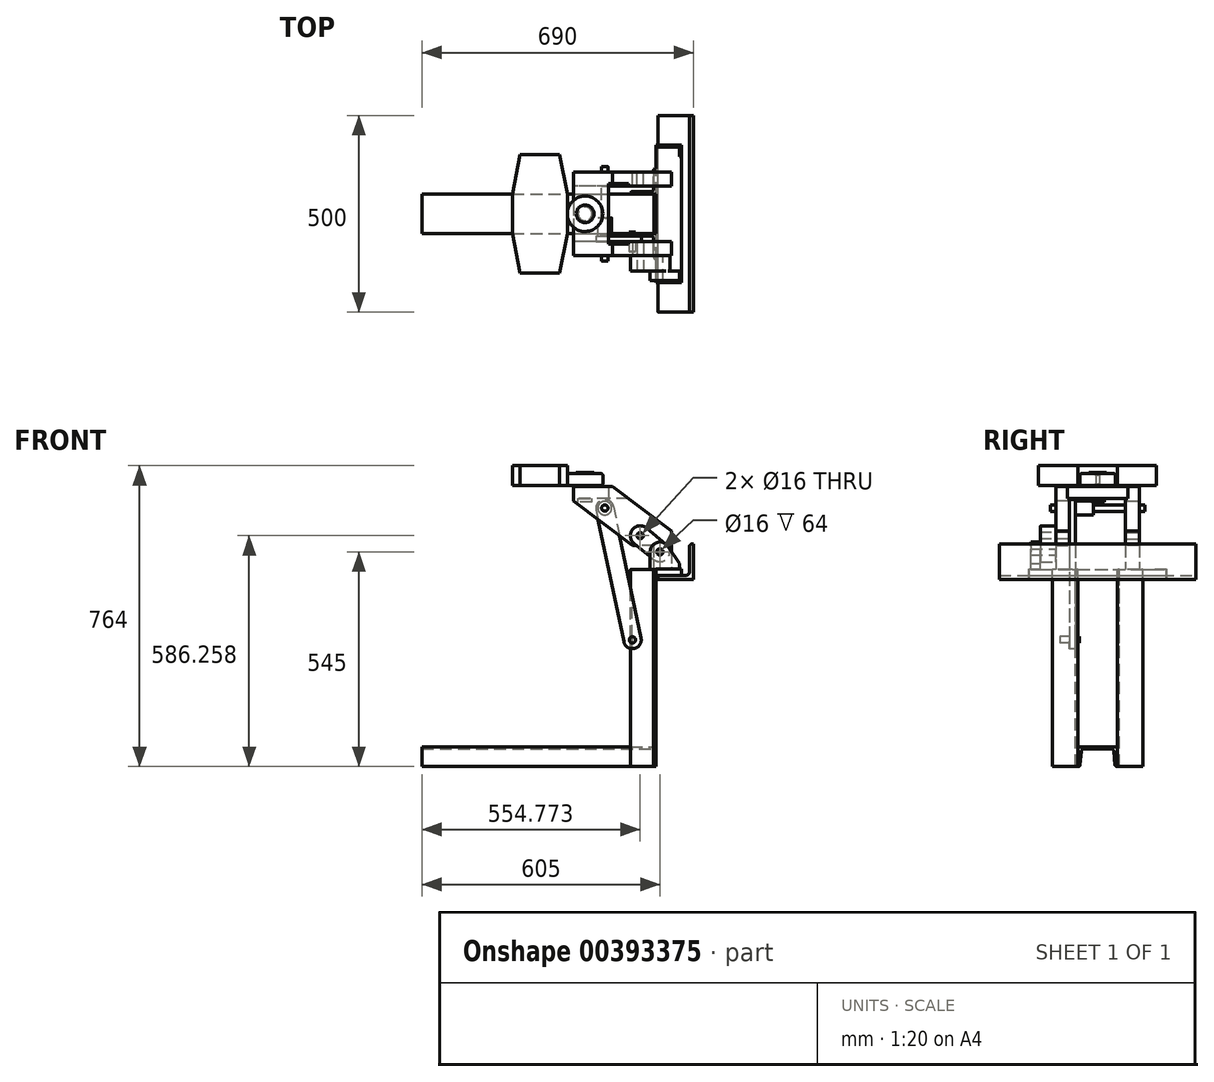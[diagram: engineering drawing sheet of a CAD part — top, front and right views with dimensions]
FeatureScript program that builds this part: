
annotation { "Feature Type Name" : "Feature", "Feature Type Description" : "" }
export const myFeature = defineFeature(function(context is Context, id is Id, definition is map)
    precondition{}
    {
        {
            var Q0;
            Q0=qCreatedBy(makeId("Front.planeOp"),FACE);
            var sketch = newSketch(context, id + "F0", { "sketchPlane" : qUnion([Q0])});
            skLineSegment(sketch, "E0", {"start": v(0, 0) * mm, "end": v(0, 90) * mm});
            skLineSegment(sketch, "E1", {"start": v(0, 90) * mm, "end": v(-3, 90) * mm});
            skLineSegment(sketch, "E2", {"start": v(-10, 83) * mm, "end": v(-10, 20) * mm});
            skLineSegment(sketch, "E3", {"start": v(-20, 10) * mm, "end": v(-83, 10) * mm});
            skLineSegment(sketch, "E4", {"start": v(-90, 3) * mm, "end": v(-90, 0) * mm});
            skLineSegment(sketch, "E5", {"start": v(-90, 0) * mm, "end": v(0, 0) * mm});
            skPoint(sketch, "E6.visualSharp", {"position": v(-10, 90) * mm});
            skArc(sketch, "E6.filletArc", {"start": v(-3, 90) * mm, "mid": v(-7.95, 87.95) * mm, "end": v(-10, 83) * mm});
            skPoint(sketch, "E7.visualSharp", {"position": v(-90, 10) * mm});
            skArc(sketch, "E7.filletArc", {"start": v(-83, 10) * mm, "mid": v(-87.95, 7.95) * mm, "end": v(-90, 3) * mm});
            skPoint(sketch, "E8.visualSharp", {"position": v(-10, 10) * mm});
            skArc(sketch, "E8.filletArc", {"start": v(-20, 10) * mm, "mid": v(-12.93, 12.93) * mm, "end": v(-10, 20) * mm});
            skLineSegment(sketch, "E9", {"start": v(-90, 0) * mm, "end": v(-95, 0) * mm});
            skLineSegment(sketch, "E10", {"start": v(-95, 0) * mm, "end": v(-95, 25) * mm});
            skLineSegment(sketch, "E11", {"start": v(-95, 25) * mm, "end": v(-30, 25) * mm});
            skLineSegment(sketch, "E12", {"start": v(-30, 25) * mm, "end": v(-30, 10) * mm});
            skLineSegment(sketch, "E13", {"start": v(-30, 10) * mm, "end": v(-90, 10) * mm});
            skLineSegment(sketch, "E14", {"start": v(-90, 0) * mm, "end": v(-90, 10) * mm});
            skLineSegment(sketch, "E15", {"start": v(-35, 25) * mm, "end": v(-35, 40) * mm});
            skLineSegment(sketch, "E16", {"start": v(-95, 25) * mm, "end": v(-110, 25) * mm});
            skLineSegment(sketch, "E17", {"start": v(-110, 25) * mm, "end": v(-110, 70) * mm});
            skCircle(sketch, "E18", {"center": v(-85, 70) * mm, "radius": 25 * mm});
            skLineSegment(sketch, "E19", {"start": v(-35, 40) * mm, "end": v(-64.19, 83.85) * mm});
            skCircle(sketch, "E20", {"center": v(-85, 70) * mm, "radius": 8 * mm});
            skSolve(sketch);
        }
        {
            var Q0;
            Q0=makeQuery(id+"F0.imprint","IMPRINT",FACE,{"disambiguationData":[TD([[makeQuery(id+"F0.imprint","IMPRINT",EDGE,{"derivedFrom":sQuery(id+"F0.wireOp",EDGE,"E0")}),1.0]])]});
            extrude(context, id + "F1", {"entities" : qUnion([Q0]), "endBound" : BoundingType.SYMMETRIC, "depth" : 500 * mm});
        }
        {
            var Q0;
            {var subQ4=sQuery(id+"F0.wireOp",EDGE,"E9");Q0=makeQuery(id+"F0.imprint","IMPRINT",FACE,{"disambiguationData":[TD([[makeQuery(id+"F0.imprint","IMPRINT",EDGE,{"derivedFrom":subQ4}),-1.0]])]});}
            extrude(context, id + "F2", {"entities" : qUnion([Q0]), "endBound" : BoundingType.SYMMETRIC, "depth" : 350 * mm});
        }
        {
            var Q0;
            {var subQ2=sQuery(id+"F0.wireOp",EDGE,"E15");Q0=makeQuery(id+"F0.imprint","IMPRINT",FACE,{"disambiguationData":[TD([[makeQuery(id+"F0.imprint","IMPRINT",EDGE,{"derivedFrom":subQ2}),1.0]])]});}
            var Q1;
            Q1=makeQuery(id+"F0.imprint","IMPRINT",FACE,{"disambiguationData":[TD([[makeQuery(id+"F0.imprint","IMPRINT",EDGE,{"derivedFrom":sQuery(id+"F0.wireOp",EDGE,"E20")}),-1.0]])]});
            extrude(context, id + "F3", {"entities" : qUnion([Q0, Q1]), "depth" : 170 * mm, "hasSecondDirection" : true, "secondDirectionOppositeDirection" : false, "secondDirectionDepth" : 145 * mm});
        }
        {
            var Q0;
            Q0=makeQuery(id+"F3.opExtrude","CAP_FACE",FACE,{"disambiguationData":[OSD([sQuery(id+"F0.wireOp",EDGE,"E11"),sQuery(id+"F0.wireOp",EDGE,"E15"),sQuery(id+"F0.wireOp",EDGE,"E16"),sQuery(id+"F0.wireOp",EDGE,"E17"),sQuery(id+"F0.wireOp",EDGE,"E18"),sQuery(id+"F0.wireOp",EDGE,"E19"),sQuery(id+"F0.wireOp",EDGE,"E20")])],"isStart":true});
            var sketch = newSketch(context, id + "F4", { "sketchPlane" : qUnion([Q0])});
            skCircle(sketch, "E21.0", {"center": v(85, 70) * mm, "radius": 8 * mm});
            skLineSegment(sketch, "E22", {"start": v(85, 70) * mm, "end": v(135.23, 111.26) * mm, "construction": true});
            skCircle(sketch, "E23", {"center": v(135.23, 111.26) * mm, "radius": 8 * mm});
            skArc(sketch, "E24", {"start": v(151.1, 91.94) * mm, "mid": v(154.55, 127.13) * mm, "end": v(119.36, 130.58) * mm});
            skArc(sketch, "E25", {"start": v(110, 70) * mm, "mid": v(62.4, 80.68) * mm, "end": v(100.87, 50.68) * mm});
            skArc(sketch, "E26.0", {"start": v(64.19, 83.85) * mm, "mid": v(92.24, 93.93) * mm, "end": v(110, 70) * mm});
            skLineSegment(sketch, "E27", {"start": v(119.36, 130.58) * mm, "end": v(69.13, 89.32) * mm});
            skLineSegment(sketch, "E28", {"start": v(151.1, 91.94) * mm, "end": v(100.87, 50.68) * mm});
            skSolve(sketch);
        }
        {
            var Q0;
            Q0=makeQuery(id+"F4.imprint","IMPRINT",FACE,{"disambiguationData":[TD([[makeQuery(id+"F4.imprint","IMPRINT",EDGE,{"derivedFrom":sQuery(id+"F4.wireOp",EDGE,"E21.0")}),1.0]])]});
            var Q1;
            Q1=makeQuery(id+"F4.imprint","IMPRINT",FACE,{"disambiguationData":[TD([[makeQuery(id+"F4.imprint","IMPRINT",EDGE,{"derivedFrom":sQuery(id+"F4.wireOp",EDGE,"E23")}),-1.0]])]});
            extrude(context, id + "F5", {"entities" : qUnion([Q0, Q1]), "depth" : 39 * mm});
        }
        {
            var Q0;
            Q0=makeQuery(id+"F5.opExtrude","CAP_FACE",FACE,{"disambiguationData":[OSD([sQuery(id+"F4.wireOp",EDGE,"E21.0"),sQuery(id+"F4.wireOp",EDGE,"E23"),sQuery(id+"F4.wireOp",EDGE,"E24"),sQuery(id+"F4.wireOp",EDGE,"E25"),sQuery(id+"F4.wireOp",EDGE,"E26.0"),sQuery(id+"F4.wireOp",EDGE,"E27"),sQuery(id+"F4.wireOp",EDGE,"E28")])],"isStart":false});
            var sketch = newSketch(context, id + "F6", { "sketchPlane" : qUnion([Q0])});
            skCircle(sketch, "E29.0", {"center": v(135.23, 111.26) * mm, "radius": 8 * mm});
            skLineSegment(sketch, "E30", {"start": v(135.23, 111.26) * mm, "end": v(225.23, 181.26) * mm, "construction": true});
            skCircle(sketch, "E31", {"center": v(225.23, 181.26) * mm, "radius": 8 * mm});
            skLineSegment(sketch, "E32", {"start": v(55.23, 86.26) * mm, "end": v(155.23, 86.26) * mm});
            skLineSegment(sketch, "E33", {"start": v(155.23, 86.26) * mm, "end": v(305.23, 198.76) * mm});
            skLineSegment(sketch, "E34", {"start": v(305.23, 198.76) * mm, "end": v(305.23, 236.26) * mm});
            skLineSegment(sketch, "E35", {"start": v(305.23, 236.26) * mm, "end": v(205.23, 236.26) * mm});
            skLineSegment(sketch, "E36", {"start": v(205.23, 236.26) * mm, "end": v(55.23, 123.76) * mm});
            skLineSegment(sketch, "E37", {"start": v(55.23, 123.76) * mm, "end": v(55.23, 86.26) * mm});
            skSolve(sketch);
        }
        {
            var Q0;
            Q0=makeQuery(id+"F6.imprint","IMPRINT",FACE,{"disambiguationData":[TD([[makeQuery(id+"F6.imprint","IMPRINT",EDGE,{"derivedFrom":sQuery(id+"F6.wireOp",EDGE,"E31")}),-1.0]])]});
            var Q1;
            Q1=makeQuery(id+"F6.imprint","IMPRINT",FACE,{"disambiguationData":[TD([[makeQuery(id+"F6.imprint","IMPRINT",EDGE,{"derivedFrom":sQuery(id+"F6.wireOp",EDGE,"E29.0")}),-1.0]])]});
            extrude(context, id + "F7", {"entities" : qUnion([Q0, Q1]), "depth" : 35 * mm});
        }
        {
            var Q0;
            Q0=makeQuery(id+"F7.opExtrude","SWEPT_FACE",FACE,{"disambiguationData":[OSD([sQuery(id+"F6.wireOp",EDGE,"E34")])]});
            var sketch = newSketch(context, id + "F8", { "sketchPlane" : qUnion([Q0])});
            skLineSegment(sketch, "E38.0", {"start": v(71, 236.26) * mm, "end": v(106, 236.26) * mm});
            skLineSegment(sketch, "E39.0", {"start": v(71, 198.76) * mm, "end": v(71, 236.26) * mm});
            skLineSegment(sketch, "E40", {"start": v(76.5, 236.26) * mm, "end": v(76.5, 206.26) * mm});
            skLineSegment(sketch, "E41", {"start": v(76.5, 206.26) * mm, "end": v(71, 206.26) * mm});
            skSolve(sketch);
        }
        {
            var Q0;
            {var subQ3=sQuery(id+"F8.wireOp",EDGE,"E40");Q0=makeQuery(id+"F8.imprint","IMPRINT",FACE,{"disambiguationData":[TD([[makeQuery(id+"F8.imprint","IMPRINT",EDGE,{"derivedFrom":subQ3}),-1.0]])]});}
            extrude(context, id + "F9", {"entities" : qUnion([Q0]), "operationType" : NewBodyOperationType.REMOVE, "endBound" : BoundingType.THROUGH_ALL, "oppositeDirection" : true, "depth" : 25 * mm});
        }
        {
            var Q0;
            Q0=makeQuery(id+"F7.opExtrude","SWEPT_FACE",FACE,{"disambiguationData":[OSD([sQuery(id+"F6.wireOp",EDGE,"E34")])]});
            var sketch = newSketch(context, id + "F10", { "sketchPlane" : qUnion([Q0])});
            skLineSegment(sketch, "E42.0", {"start": v(76.5, 236.26) * mm, "end": v(76.5, 206.26) * mm});
            skLineSegment(sketch, "E43.0", {"start": v(76.5, 206.26) * mm, "end": v(71, 206.26) * mm});
            skLineSegment(sketch, "E44", {"start": v(76.5, 236.26) * mm, "end": v(-76.5, 236.26) * mm});
            skLineSegment(sketch, "E45", {"start": v(-76.5, 236.26) * mm, "end": v(-76.5, 206.26) * mm});
            skLineSegment(sketch, "E46", {"start": v(-76.5, 206.26) * mm, "end": v(71, 206.26) * mm});
            skPoint(sketch, "E47", {"position": v(0, 236.26) * mm});
            skSolve(sketch);
        }
        {
            var Q0;
            Q0=makeQuery(id+"F10.imprint","IMPRINT",FACE,{"disambiguationData":[TD([[makeQuery(id+"F10.imprint","IMPRINT",EDGE,{"derivedFrom":sQuery(id+"F10.wireOp",EDGE,"E42.0")}),-1.0]])]});
            extrude(context, id + "F11", {"entities" : qUnion([Q0]), "oppositeDirection" : true, "depth" : 90 * mm});
        }
        {
            var Q0;
            Q0=makeQuery(id+"F11.opExtrude","SWEPT_FACE",FACE,{"disambiguationData":[OSD([sQuery(id+"F10.wireOp",EDGE,"E44")])]});
            var sketch = newSketch(context, id + "F12", { "sketchPlane" : qUnion([Q0])});
            skCircle(sketch, "E48", {"center": v(-275.23, 0) * mm, "radius": 17.5 * mm});
            skSolve(sketch);
        }
        {
            var Q0;
            Q0=makeQuery(id+"F12.imprint","IMPRINT",FACE,{"disambiguationData":[TD([[makeQuery(id+"F12.imprint","IMPRINT",EDGE,{"derivedFrom":sQuery(id+"F12.wireOp",EDGE,"E48")}),1.0]])]});
            extrude(context, id + "F13", {"entities" : qUnion([Q0]), "operationType" : NewBodyOperationType.REMOVE, "endBound" : BoundingType.THROUGH_ALL, "oppositeDirection" : true, "depth" : 25 * mm});
        }
        {
            var Q0;
            Q0=makeQuery(id+"F11.opExtrude","SWEPT_FACE",FACE,{"disambiguationData":[OSD([sQuery(id+"F10.wireOp",EDGE,"E44")])]});
            var sketch = newSketch(context, id + "F14", { "sketchPlane" : qUnion([Q0])});
            skCircle(sketch, "E49.0", {"center": v(-275.23, 0) * mm, "radius": 17.5 * mm});
            skCircle(sketch, "E50", {"center": v(-275.23, 0) * mm, "radius": 22.5 * mm});
            skCircle(sketch, "E51", {"center": v(-275.23, 0) * mm, "radius": 45 * mm});
            skSolve(sketch);
        }
        {
            var Q0;
            Q0=makeQuery(id+"F14.imprint","IMPRINT",FACE,{"disambiguationData":[TD([[makeQuery(id+"F14.imprint","IMPRINT",EDGE,{"derivedFrom":sQuery(id+"F14.wireOp",EDGE,"E49.0")}),1.0]])]});
            extrude(context, id + "F15", {"entities" : qUnion([Q0]), "oppositeDirection" : true, "depth" : 40 * mm});
        }
        {
            var Q0;
            Q0=makeQuery(id+"F14.imprint","IMPRINT",FACE,{"disambiguationData":[TD([[makeQuery(id+"F14.imprint","IMPRINT",EDGE,{"derivedFrom":sQuery(id+"F14.wireOp",EDGE,"E49.0")}),1.0]])]});
            var Q1;
            Q1=makeQuery(id+"F14.imprint","IMPRINT",FACE,{"disambiguationData":[TD([[makeQuery(id+"F14.imprint","IMPRINT",EDGE,{"derivedFrom":sQuery(id+"F14.wireOp",EDGE,"E49.0")}),-1.0]])]});
            extrude(context, id + "F16", {"entities" : qUnion([Q0, Q1]), "operationType" : NewBodyOperationType.ADD, "depth" : 35 * mm});
        }
        {
            var Q0;
            Q0=makeQuery(id+"F14.imprint","IMPRINT",FACE,{"disambiguationData":[TD([[makeQuery(id+"F14.imprint","IMPRINT",EDGE,{"derivedFrom":sQuery(id+"F14.wireOp",EDGE,"E50")}),-1.0]])]});
            var Q1;
            {var subQ0=sQuery(id+"F14.wireOp",EDGE,"E51");var subQ1=makeQuery(id+"F11.opExtrude","CAP_EDGE",EDGE,{"disambiguationData":[OSD([sQuery(id+"F10.wireOp",EDGE,"E44")])],"isStart":true});var subQ2=makeQuery(id+"F14.imprint","INTERSECT",VERTEX,{"disambiguationData":[OD(0.0)],"derivedFrom":[subQ1,subQ0]});Q1=makeQuery(id+"F14.imprint","IMPRINT",FACE,{"disambiguationData":[TD([[makeQuery(id+"F14.imprint","IMPRINT",EDGE,{"disambiguationData":[TD([[subQ2,1.0]])],"derivedFrom":subQ0}),1.0]])]});}
            var Q2;
            Q2=makeQuery(id+"F14.imprint","IMPRINT",FACE,{"disambiguationData":[TD([[makeQuery(id+"F14.imprint","IMPRINT",EDGE,{"derivedFrom":sQuery(id+"F14.wireOp",EDGE,"E49.0")}),-1.0]])]});
            var Q3;
            Q3=makeQuery(id+"F14.imprint","IMPRINT",FACE,{"disambiguationData":[TD([[makeQuery(id+"F14.imprint","IMPRINT",EDGE,{"derivedFrom":sQuery(id+"F14.wireOp",EDGE,"E49.0")}),1.0]])]});
            extrude(context, id + "F17", {"entities" : qUnion([Q0, Q1, Q2, Q3]), "operationType" : NewBodyOperationType.ADD, "depth" : 33 * mm, "hasSecondDirection" : true, "secondDirectionOppositeDirection" : false, "secondDirectionDepth" : 2 * mm});
        }
        {
            var Q0;
            Q0=makeQuery(id+"F17.opExtrude","CAP_EDGE",EDGE,{"disambiguationData":[OSD([sQuery(id+"F14.wireOp",EDGE,"E51")])],"isStart":false});
            var Q1;
            Q1=makeQuery(id+"F17.opExtrude","CAP_EDGE",EDGE,{"disambiguationData":[OSD([sQuery(id+"F14.wireOp",EDGE,"E51")])],"isStart":true});
            fillet(context, id + "F18", {"entities" : qUnion([Q0, Q1]), "radius" : 5 * mm, "tangentPropagation" : true, "allowEdgeOverflow" : false});
        }
        {
            var Q0;
            Q0=makeQuery(id+"F7.opExtrude","CAP_FACE",FACE,{"disambiguationData":[OSD([sQuery(id+"F6.wireOp",EDGE,"E29.0"),sQuery(id+"F6.wireOp",EDGE,"E31"),sQuery(id+"F6.wireOp",EDGE,"E32"),sQuery(id+"F6.wireOp",EDGE,"E33"),sQuery(id+"F6.wireOp",EDGE,"E34"),sQuery(id+"F6.wireOp",EDGE,"E35"),sQuery(id+"F6.wireOp",EDGE,"E36"),sQuery(id+"F6.wireOp",EDGE,"E37")])],"isStart":false});
            var sketch = newSketch(context, id + "F19", { "sketchPlane" : qUnion([Q0])});
            skLineSegment(sketch, "E52", {"start": v(225.23, 181.26) * mm, "end": v(155, -153.45) * mm, "construction": true});
            skCircle(sketch, "E53.0", {"center": v(85, 70) * mm, "radius": 8 * mm});
            skCircle(sketch, "E54", {"center": v(225.23, 181.26) * mm, "radius": 8 * mm});
            skArc(sketch, "E55", {"start": v(247.25, 176.64) * mm, "mid": v(229.85, 203.28) * mm, "end": v(203.2, 185.88) * mm});
            skCircle(sketch, "E56", {"center": v(155, -153.45) * mm, "radius": 8 * mm});
            skArc(sketch, "E57", {"start": v(132.98, -148.83) * mm, "mid": v(150.38, -175.47) * mm, "end": v(177.02, -158.07) * mm});
            skLineSegment(sketch, "E58", {"start": v(203.2, 185.88) * mm, "end": v(132.98, -148.83) * mm});
            skLineSegment(sketch, "E59", {"start": v(247.25, 176.64) * mm, "end": v(177.02, -158.07) * mm});
            skSolve(sketch);
        }
        {
            var Q0;
            Q0=makeQuery(id+"F19.imprint","IMPRINT",FACE,{"disambiguationData":[TD([[makeQuery(id+"F19.imprint","IMPRINT",EDGE,{"derivedFrom":sQuery(id+"F19.wireOp",EDGE,"E56")}),-1.0]])]});
            var Q1;
            Q1=makeQuery(id+"F19.imprint","IMPRINT",FACE,{"disambiguationData":[TD([[makeQuery(id+"F19.imprint","IMPRINT",EDGE,{"derivedFrom":sQuery(id+"F19.wireOp",EDGE,"E54")}),-1.0]])]});
            extrude(context, id + "F20", {"entities" : qUnion([Q0, Q1]), "depth" : 15 * mm});
        }
        {
            var Q0;
            Q0=qCreatedBy(makeId("Front.planeOp"),FACE);
            var sketch = newSketch(context, id + "F21", { "sketchPlane" : qUnion([Q0])});
            skCircle(sketch, "E60.0", {"center": v(-225.23, 181.26) * mm, "radius": 8 * mm});
            skCircle(sketch, "E61", {"center": v(-225.23, 181.26) * mm, "radius": 17.5 * mm});
            skSolve(sketch);
        }
        {
            var Q0;
            Q0=makeQuery(id+"F21.imprint","IMPRINT",FACE,{"disambiguationData":[TD([[makeQuery(id+"F21.imprint","IMPRINT",EDGE,{"derivedFrom":sQuery(id+"F21.wireOp",EDGE,"E60.0")}),1.0]])]});
            extrude(context, id + "F22", {"entities" : qUnion([Q0]), "endBound" : BoundingType.SYMMETRIC, "depth" : 240 * mm});
        }
        {
            var Q0;
            Q0=makeQuery(id+"F21.imprint","IMPRINT",FACE,{"disambiguationData":[TD([[makeQuery(id+"F21.imprint","IMPRINT",EDGE,{"derivedFrom":sQuery(id+"F21.wireOp",EDGE,"E60.0")}),-1.0]])]});
            var Q1;
            Q1=makeQuery(id+"F7.opExtrude","CAP_FACE",FACE,{"disambiguationData":[OSD([sQuery(id+"F6.wireOp",EDGE,"E29.0"),sQuery(id+"F6.wireOp",EDGE,"E31"),sQuery(id+"F6.wireOp",EDGE,"E32"),sQuery(id+"F6.wireOp",EDGE,"E33"),sQuery(id+"F6.wireOp",EDGE,"E34"),sQuery(id+"F6.wireOp",EDGE,"E35"),sQuery(id+"F6.wireOp",EDGE,"E36"),sQuery(id+"F6.wireOp",EDGE,"E37")])],"isStart":false});
            extrude(context, id + "F23", {"entities" : qUnion([Q0]), "endBound" : BoundingType.UP_TO_SURFACE, "endBoundEntityFace" : qUnion([Q1]), "depth" : 25 * mm, "hasSecondDirection" : true, "secondDirectionOppositeDirection" : false, "secondDirectionDepth" : 10.5 * mm});
        }
        {
            var Q0;
            Q0=makeQuery(id+"F11.opExtrude","SWEPT_FACE",FACE,{"disambiguationData":[OSD([sQuery(id+"F10.wireOp",EDGE,"E45")])]});
            var sketch = newSketch(context, id + "F24", { "sketchPlane" : qUnion([Q0])});
            skLineSegment(sketch, "E62.0", {"start": v(205.23, 236.26) * mm, "end": v(305.23, 236.26) * mm});
            skLineSegment(sketch, "E63.0", {"start": v(165.23, 206.26) * mm, "end": v(305.23, 206.26) * mm});
            skLineSegment(sketch, "E64.0", {"start": v(205.23, 236.26) * mm, "end": v(165.23, 206.26) * mm});
            skLineSegment(sketch, "E65.0", {"start": v(305.23, 236.26) * mm, "end": v(305.23, 206.26) * mm});
            skLineSegment(sketch, "E66.0", {"start": v(305.23, 198.76) * mm, "end": v(305.23, 206.26) * mm});
            skLineSegment(sketch, "E67.0", {"start": v(155.23, 86.26) * mm, "end": v(305.23, 198.76) * mm});
            skLineSegment(sketch, "E68.0", {"start": v(205.23, 236.26) * mm, "end": v(55.23, 123.76) * mm});
            skLineSegment(sketch, "E69.0", {"start": v(55.23, 123.76) * mm, "end": v(55.23, 86.26) * mm});
            skLineSegment(sketch, "E70.0", {"start": v(55.23, 86.26) * mm, "end": v(155.23, 86.26) * mm});
            skCircle(sketch, "E71.0", {"center": v(225.23, 181.26) * mm, "radius": 8 * mm});
            skCircle(sketch, "E72.0", {"center": v(135.23, 111.26) * mm, "radius": 8 * mm});
            skSolve(sketch);
        }
        {
            var Q0;
            {var subQ0=sQuery(id+"F24.wireOp",EDGE,"E66.0");Q0=makeQuery(id+"F24.imprint","IMPRINT",FACE,{"disambiguationData":[TD([[makeQuery(id+"F24.imprint","IMPRINT",EDGE,{"derivedFrom":subQ0}),1.0]])]});}
            extrude(context, id + "F25", {"entities" : qUnion([Q0]), "oppositeDirection" : true, "depth" : 5.5 * mm});
        }
        {
            var Q0;
            {var subQ0=sQuery(id+"F24.wireOp",EDGE,"E66.0");Q0=makeQuery(id+"F24.imprint","IMPRINT",FACE,{"disambiguationData":[TD([[makeQuery(id+"F24.imprint","IMPRINT",EDGE,{"derivedFrom":subQ0}),1.0]])]});}
            var Q1;
            {var subQ1=makeQuery(id+"F11.opExtrude","CAP_EDGE",EDGE,{"disambiguationData":[OSD([sQuery(id+"F10.wireOp",EDGE,"E45")])],"isStart":false});Q1=makeQuery(id+"F24.imprint","IMPRINT",FACE,{"disambiguationData":[TD([[makeQuery(id+"F24.imprint","IMPRINT",EDGE,{"derivedFrom":subQ1}),-1.0]])]});}
            var Q2;
            {var subQ0=sQuery(id+"F24.wireOp",EDGE,"E65.0");Q2=makeQuery(id+"F24.imprint","IMPRINT",FACE,{"disambiguationData":[TD([[makeQuery(id+"F24.imprint","IMPRINT",EDGE,{"derivedFrom":subQ0}),-1.0]])]});}
            extrude(context, id + "F26", {"entities" : qUnion([Q0, Q1, Q2]), "operationType" : NewBodyOperationType.ADD, "depth" : 29.5 * mm});
        }
        {
            var Q0;
            Q0=makeQuery(id+"F2.opExtrude","SWEPT_FACE",FACE,{"disambiguationData":[OSD([sQuery(id+"F0.wireOp",EDGE,"E11")])]});
            var sketch = newSketch(context, id + "F27", { "sketchPlane" : qUnion([Q0])});
            skLineSegment(sketch, "E73.0", {"start": v(-35, -170) * mm, "end": v(-110, -170) * mm});
            skLineSegment(sketch, "E74.0", {"start": v(-35, -170) * mm, "end": v(-35, -145) * mm});
            skLineSegment(sketch, "E75.0", {"start": v(-30, -175) * mm, "end": v(-30, 175) * mm});
            skLineSegment(sketch, "E76.0", {"start": v(-95, -175) * mm, "end": v(-30, -175) * mm});
            skLineSegment(sketch, "E77.0", {"start": v(-95, -175) * mm, "end": v(-95, 175) * mm});
            skLineSegment(sketch, "E78.0", {"start": v(-95, 175) * mm, "end": v(-30, 175) * mm});
            skLineSegment(sketch, "E79", {"start": v(-35, 145) * mm, "end": v(-35, 170) * mm});
            skLineSegment(sketch, "E80", {"start": v(-35, 170) * mm, "end": v(-110, 170) * mm});
            skLineSegment(sketch, "E81", {"start": v(-35, -145) * mm, "end": v(-30, -145) * mm});
            skLineSegment(sketch, "E82", {"start": v(-35, 145) * mm, "end": v(-30, 145) * mm});
            skSolve(sketch);
        }
        {
            var Q0;
            {var subQ3=sQuery(id+"F27.wireOp",EDGE,"E74.0");Q0=makeQuery(id+"F27.imprint","IMPRINT",FACE,{"disambiguationData":[TD([[makeQuery(id+"F27.imprint","IMPRINT",EDGE,{"derivedFrom":subQ3}),-1.0]])]});}
            var Q1;
            {var subQ1=sQuery(id+"F27.wireOp",EDGE,"E78.0");Q1=makeQuery(id+"F27.imprint","IMPRINT",FACE,{"disambiguationData":[TD([[makeQuery(id+"F27.imprint","IMPRINT",EDGE,{"derivedFrom":subQ1}),-1.0]])]});}
            extrude(context, id + "F28", {"entities" : qUnion([Q0, Q1]), "operationType" : NewBodyOperationType.ADD, "depth" : 1 * mm});
        }
        {
            var Q0;
            Q0=makeQuery(id+"F2.opExtrude","SWEPT_FACE",FACE,{"disambiguationData":[OSD([sQuery(id+"F0.wireOp",EDGE,"E11")])]});
            var sketch = newSketch(context, id + "F29", { "sketchPlane" : qUnion([Q0])});
            skLineSegment(sketch, "E83.0", {"start": v(-95, -50) * mm, "end": v(-95, 115) * mm});
            skLineSegment(sketch, "E84", {"start": v(-95, 50) * mm, "end": v(-95, -50) * mm, "construction": true});
            skPoint(sketch, "E85", {"position": v(-95, 0) * mm});
            skLineSegment(sketch, "E86", {"start": v(-95, 50) * mm, "end": v(-160, 50) * mm});
            skLineSegment(sketch, "E87", {"start": v(-160, 50) * mm, "end": v(-160, 52) * mm});
            skLineSegment(sketch, "E88", {"start": v(-156, 56) * mm, "end": v(-109, 56) * mm});
            skLineSegment(sketch, "E89", {"start": v(-101, 64) * mm, "end": v(-101, 111) * mm});
            skLineSegment(sketch, "E90", {"start": v(-97, 115) * mm, "end": v(-95, 115) * mm});
            skPoint(sketch, "E91.orphan", {"position": v(-95, 170) * mm});
            skPoint(sketch, "E92.orphan", {"position": v(-95, -170) * mm});
            skPoint(sketch, "E93.visualSharp", {"position": v(-101, 56) * mm});
            skArc(sketch, "E93.filletArc", {"start": v(-109, 56) * mm, "mid": v(-103.34, 58.34) * mm, "end": v(-101, 64) * mm});
            skPoint(sketch, "E94.visualSharp", {"position": v(-101, 115) * mm});
            skArc(sketch, "E94.filletArc", {"start": v(-97, 115) * mm, "mid": v(-99.83, 113.83) * mm, "end": v(-101, 111) * mm});
            skPoint(sketch, "E95.visualSharp", {"position": v(-160, 56) * mm});
            skArc(sketch, "E95.filletArc", {"start": v(-156, 56) * mm, "mid": v(-158.83, 54.83) * mm, "end": v(-160, 52) * mm});
            skLineSegment(sketch, "E96", {"start": v(-95, -50) * mm, "end": v(-160, -50) * mm});
            skLineSegment(sketch, "E97", {"start": v(-160, -50) * mm, "end": v(-160, -52) * mm});
            skLineSegment(sketch, "E98", {"start": v(-156, -56) * mm, "end": v(-109, -56) * mm});
            skLineSegment(sketch, "E99", {"start": v(-101, -64) * mm, "end": v(-101, -111) * mm});
            skLineSegment(sketch, "E100", {"start": v(-97, -115) * mm, "end": v(-95, -115) * mm});
            skLineSegment(sketch, "E101", {"start": v(-95, -115) * mm, "end": v(-95, -50) * mm});
            skPoint(sketch, "E102.visualSharp", {"position": v(-101, -56) * mm});
            skArc(sketch, "E102.filletArc", {"start": v(-101, -64) * mm, "mid": v(-103.34, -58.34) * mm, "end": v(-109, -56) * mm});
            skPoint(sketch, "E103.visualSharp", {"position": v(-160, -56) * mm});
            skArc(sketch, "E103.filletArc", {"start": v(-160, -52) * mm, "mid": v(-158.83, -54.83) * mm, "end": v(-156, -56) * mm});
            skPoint(sketch, "E104.visualSharp", {"position": v(-101, -115) * mm});
            skArc(sketch, "E104.filletArc", {"start": v(-101, -111) * mm, "mid": v(-99.83, -113.83) * mm, "end": v(-97, -115) * mm});
            skSolve(sketch);
        }
        {
            var Q0;
            {var subQ0=sQuery(id+"F29.wireOp",EDGE,"E86");Q0=makeQuery(id+"F29.imprint","IMPRINT",FACE,{"disambiguationData":[TD([[makeQuery(id+"F29.imprint","IMPRINT",EDGE,{"derivedFrom":subQ0}),-1.0]])]});}
            var Q1;
            Q1=makeQuery(id+"F29.imprint","IMPRINT",FACE,{"disambiguationData":[TD([[makeQuery(id+"F29.imprint","IMPRINT",EDGE,{"derivedFrom":sQuery(id+"F29.wireOp",EDGE,"E96")}),1.0]])]});
            extrude(context, id + "F30", {"entities" : qUnion([Q0, Q1]), "operationType" : NewBodyOperationType.ADD, "oppositeDirection" : true, "depth" : 500 * mm});
        }
        {
            var Q0;
            Q0=makeQuery(id+"F30.opExtrude","SWEPT_FACE",FACE,{"disambiguationData":[OSD([sQuery(id+"F29.wireOp",EDGE,"E98")])]});
            var sketch = newSketch(context, id + "F31", { "sketchPlane" : qUnion([Q0])});
            skCircle(sketch, "E105.0", {"center": v(-155, -153.45) * mm, "radius": 8 * mm});
            skSolve(sketch);
        }
        {
            var Q0;
            {var subQ0=sQuery(id+"F31.wireOp",EDGE,"E105.0");var subQ1=makeQuery(id+"F30.opExtrude","SWEPT_EDGE",EDGE,{"disambiguationData":[OSD([sQuery(id+"F29.wireOp",EDGE,"E98"),sQuery(id+"F29.wireOp",EDGE,"E103.filletArc")])]});var subQ2=makeQuery(id+"F31.imprint","INTERSECT",VERTEX,{"disambiguationData":[OD(0.0)],"derivedFrom":[subQ1,subQ0]});Q0=makeQuery(id+"F31.imprint","IMPRINT",FACE,{"disambiguationData":[TD([[makeQuery(id+"F31.imprint","IMPRINT",EDGE,{"disambiguationData":[TD([[subQ2,1.0]])],"derivedFrom":subQ0}),1.0]])]});}
            var Q1;
            {var subQ0=sQuery(id+"F31.wireOp",EDGE,"E105.0");var subQ1=makeQuery(id+"F30.opExtrude","SWEPT_EDGE",EDGE,{"disambiguationData":[OSD([sQuery(id+"F29.wireOp",EDGE,"E98"),sQuery(id+"F29.wireOp",EDGE,"E103.filletArc")])]});var subQ2=makeQuery(id+"F31.imprint","INTERSECT",VERTEX,{"disambiguationData":[OD(0.0)],"derivedFrom":[subQ1,subQ0]});Q1=makeQuery(id+"F31.imprint","IMPRINT",FACE,{"disambiguationData":[TD([[makeQuery(id+"F31.imprint","IMPRINT",EDGE,{"disambiguationData":[TD([[subQ2,-1.0]])],"derivedFrom":subQ0}),1.0]])]});}
            extrude(context, id + "F32", {"entities" : qUnion([Q0, Q1]), "operationType" : NewBodyOperationType.REMOVE, "endBound" : BoundingType.THROUGH_ALL, "oppositeDirection" : true, "depth" : 25 * mm});
        }
        {
            var Q0;
            Q0=makeQuery(id+"F30.opExtrude","SWEPT_FACE",FACE,{"disambiguationData":[OSD([sQuery(id+"F29.wireOp",EDGE,"E101")])]});
            var sketch = newSketch(context, id + "F33", { "sketchPlane" : qUnion([Q0])});
            skLineSegment(sketch, "E106.0", {"start": v(-50, -475) * mm, "end": v(-50, -425) * mm});
            skLineSegment(sketch, "E107.0", {"start": v(50, -475) * mm, "end": v(50, -425) * mm});
            skLineSegment(sketch, "E108", {"start": v(-50, -425) * mm, "end": v(50, -425) * mm});
            skLineSegment(sketch, "E109", {"start": v(-50, -475) * mm, "end": v(-48.35, -475) * mm});
            skLineSegment(sketch, "E110", {"start": v(-44.37, -471.35) * mm, "end": v(-41.39, -437.3) * mm});
            skLineSegment(sketch, "E111", {"start": v(-33.42, -430) * mm, "end": v(33.42, -430) * mm});
            skLineSegment(sketch, "E112", {"start": v(41.39, -437.3) * mm, "end": v(44.37, -471.35) * mm});
            skLineSegment(sketch, "E113", {"start": v(48.35, -475) * mm, "end": v(50, -475) * mm});
            skPoint(sketch, "E114.visualSharp", {"position": v(-40.75, -430) * mm});
            skArc(sketch, "E114.filletArc", {"start": v(-33.42, -430) * mm, "mid": v(-38.82, -432.1) * mm, "end": v(-41.39, -437.3) * mm});
            skPoint(sketch, "E115.visualSharp", {"position": v(40.75, -430) * mm});
            skArc(sketch, "E115.filletArc", {"start": v(41.39, -437.3) * mm, "mid": v(38.82, -432.1) * mm, "end": v(33.42, -430) * mm});
            skPoint(sketch, "E116.visualSharp", {"position": v(-44.69, -475) * mm});
            skArc(sketch, "E116.filletArc", {"start": v(-48.35, -475) * mm, "mid": v(-45.65, -473.95) * mm, "end": v(-44.37, -471.35) * mm});
            skPoint(sketch, "E117.visualSharp", {"position": v(44.69, -475) * mm});
            skArc(sketch, "E117.filletArc", {"start": v(44.37, -471.35) * mm, "mid": v(45.65, -473.95) * mm, "end": v(48.35, -475) * mm});
            skPoint(sketch, "E118.orphan", {"position": v(-50, 0) * mm});
            skPoint(sketch, "E119.orphan", {"position": v(50, 0) * mm});
            skLineSegment(sketch, "E120", {"start": v(-50, -450) * mm, "end": v(50, -450) * mm, "construction": true});
            skPoint(sketch, "E121", {"position": v(-42.5, -450) * mm});
            skSolve(sketch);
        }
        {
            var Q0;
            Q0=makeQuery(id+"F33.imprint","IMPRINT",FACE,{"disambiguationData":[TD([[makeQuery(id+"F33.imprint","IMPRINT",EDGE,{"derivedFrom":sQuery(id+"F33.wireOp",EDGE,"E106.0")}),-1.0]])]});
            extrude(context, id + "F34", {"entities" : qUnion([Q0]), "operationType" : NewBodyOperationType.ADD, "oppositeDirection" : true, "depth" : 595 * mm, "hasSecondDirection" : true, "secondDirectionOppositeDirection" : true, "secondDirectionDepth" : 5 * mm});
        }
        {
            var Q0;
            Q0=qCreatedBy(makeId("Front.planeOp"),FACE);
            var sketch = newSketch(context, id + "F35", { "sketchPlane" : qUnion([Q0])});
            skLineSegment(sketch, "E122.0", {"start": v(-690, -425) * mm, "end": v(-160, -425) * mm});
            skLineSegment(sketch, "E123.0", {"start": v(-90, 0) * mm, "end": v(-90, 10) * mm});
            skLineSegment(sketch, "E124.0", {"start": v(-30, 10) * mm, "end": v(-90, 10) * mm});
            skLineSegment(sketch, "E125", {"start": v(-390, -425) * mm, "end": v(-390, 239.47) * mm, "construction": true});
            skLineSegment(sketch, "E126.bottom", {"start": v(-460, 289) * mm, "end": v(-320, 289) * mm});
            skLineSegment(sketch, "E126.top", {"start": v(-460, 239) * mm, "end": v(-320, 239) * mm});
            skLineSegment(sketch, "E126.left", {"start": v(-460, 289) * mm, "end": v(-460, 239) * mm});
            skLineSegment(sketch, "E126.right", {"start": v(-320, 289) * mm, "end": v(-320, 239) * mm});
            skPoint(sketch, "E127", {"position": v(-390, 289) * mm});
            skLineSegment(sketch, "E128.bottom", {"start": v(-396.67, 239) * mm, "end": v(-383.33, 239) * mm});
            skLineSegment(sketch, "E128.top", {"start": v(-396.67, -425) * mm, "end": v(-383.33, -425) * mm});
            skLineSegment(sketch, "E128.left", {"start": v(-396.67, 239) * mm, "end": v(-396.67, -425) * mm});
            skLineSegment(sketch, "E128.right", {"start": v(-383.33, 239) * mm, "end": v(-383.33, -425) * mm});
            skPoint(sketch, "E129", {"position": v(-390, 239) * mm});
            skSolve(sketch);
        }
        {
            var Q0;
            Q0=makeQuery(id+"F35.imprint","IMPRINT",FACE,{"disambiguationData":[TD([[makeQuery(id+"F35.imprint","IMPRINT",EDGE,{"derivedFrom":sQuery(id+"F35.wireOp",EDGE,"E126.bottom")}),-1.0]])]});
            var Q1;
            Q1=makeQuery(id+"F35.imprint","IMPRINT",FACE,{"disambiguationData":[TD([[makeQuery(id+"F35.imprint","IMPRINT",EDGE,{"derivedFrom":sQuery(id+"F35.wireOp",EDGE,"E128.bottom")}),-1.0]])]});
            extrude(context, id + "F36", {"entities" : qUnion([Q0, Q1]), "operationType" : NewBodyOperationType.ADD, "endBound" : BoundingType.SYMMETRIC, "depth" : 2 * mm});
        }
        {
            var Q0;
            Q0=makeQuery(id+"F35.imprint","IMPRINT",FACE,{"disambiguationData":[TD([[makeQuery(id+"F35.imprint","IMPRINT",EDGE,{"derivedFrom":sQuery(id+"F35.wireOp",EDGE,"E126.bottom")}),-1.0]])]});
            extrude(context, id + "F37", {"entities" : qUnion([Q0]), "operationType" : NewBodyOperationType.ADD, "endBound" : BoundingType.SYMMETRIC, "depth" : 300 * mm});
        }
        {
            var Q0;
            {var subQ0=sQuery(id+"F35.wireOp",EDGE,"E126.bottom");Q0=makeQuery(id+"F37.boolean.opBoolean","MERGE",FACE,{"derivedFrom":[makeQuery(id+"F36.opExtrude","SWEPT_FACE",FACE,{"disambiguationData":[OSD([subQ0])]}),makeQuery(id+"F37.opExtrude","SWEPT_FACE",FACE,{"disambiguationData":[OSD([subQ0])]})]});}
            var sketch = newSketch(context, id + "F38", { "sketchPlane" : qUnion([Q0])});
            skLineSegment(sketch, "E130.0", {"start": v(-460, 150) * mm, "end": v(-320, 150) * mm});
            skLineSegment(sketch, "E131.0", {"start": v(-690, 50) * mm, "end": v(-160, 50) * mm});
            skLineSegment(sketch, "E132.0", {"start": v(-690, -50) * mm, "end": v(-160, -50) * mm});
            skLineSegment(sketch, "E133", {"start": v(-340, 150) * mm, "end": v(-340, -150) * mm, "construction": true});
            skLineSegment(sketch, "E134", {"start": v(-440, 150) * mm, "end": v(-440, -150) * mm, "construction": true});
            skLineSegment(sketch, "E135", {"start": v(-340, 150) * mm, "end": v(-320, 50) * mm});
            skLineSegment(sketch, "E136", {"start": v(-340, -150) * mm, "end": v(-320, -50) * mm});
            skLineSegment(sketch, "E137", {"start": v(-440, 150) * mm, "end": v(-460, 50) * mm});
            skLineSegment(sketch, "E138", {"start": v(-440, -150) * mm, "end": v(-460, -50) * mm});
            skSolve(sketch);
        }
        {
            var Q0;
            {var subQ5=sQuery(id+"F38.wireOp",EDGE,"E135");Q0=makeQuery(id+"F38.imprint","IMPRINT",FACE,{"disambiguationData":[TD([[makeQuery(id+"F38.imprint","IMPRINT",EDGE,{"derivedFrom":subQ5}),1.0]])]});}
            var Q1;
            {var subQ5=sQuery(id+"F38.wireOp",EDGE,"E137");Q1=makeQuery(id+"F38.imprint","IMPRINT",FACE,{"disambiguationData":[TD([[makeQuery(id+"F38.imprint","IMPRINT",EDGE,{"derivedFrom":subQ5}),-1.0]])]});}
            var Q2;
            {var subQ0=sQuery(id+"F38.wireOp",EDGE,"E138");Q2=makeQuery(id+"F38.imprint","IMPRINT",FACE,{"disambiguationData":[TD([[makeQuery(id+"F38.imprint","IMPRINT",EDGE,{"derivedFrom":subQ0}),1.0]])]});}
            var Q3;
            {var subQ0=sQuery(id+"F38.wireOp",EDGE,"E136");Q3=makeQuery(id+"F38.imprint","IMPRINT",FACE,{"disambiguationData":[TD([[makeQuery(id+"F38.imprint","IMPRINT",EDGE,{"derivedFrom":subQ0}),-1.0]])]});}
            var Q4;
            {var subQ0=sQuery(id+"F35.wireOp",EDGE,"E128.bottom");var subQ1=sQuery(id+"F35.wireOp",EDGE,"E126.top");Q4=makeQuery(id+"F37.boolean.opBoolean","MERGE",FACE,{"derivedFrom":[makeQuery(id+"F36.opExtrude","SWEPT_FACE",FACE,{"disambiguationData":[OSD([subQ1]),TDD([makeQuery(id+"F35.imprint","IMPRINT",EDGE,{"disambiguationData":[TD([[makeQuery(id+"F35.imprint","INTERSECT",VERTEX,{"derivedFrom":[subQ1,sQuery(id+"F35.wireOp",EDGE,"E126.left")]}),-1.0]])],"derivedFrom":subQ1})])]}),makeQuery(id+"F36.opExtrude","SWEPT_FACE",FACE,{"disambiguationData":[OSD([subQ1]),TDD([makeQuery(id+"F35.imprint","IMPRINT",EDGE,{"disambiguationData":[TD([[makeQuery(id+"F35.imprint","INTERSECT",VERTEX,{"derivedFrom":[subQ1,sQuery(id+"F35.wireOp",EDGE,"E126.right")]}),1.0]])],"derivedFrom":subQ1})])]}),makeQuery(id+"F37.opExtrude","SWEPT_FACE",FACE,{"disambiguationData":[OSD([subQ1,subQ0])]})]});}
            extrude(context, id + "F39", {"entities" : qUnion([Q0, Q1, Q2, Q3]), "operationType" : NewBodyOperationType.REMOVE, "endBound" : BoundingType.UP_TO_SURFACE, "oppositeDirection" : true, "endBoundEntityFace" : qUnion([Q4]), "depth" : 25 * mm});
        }
        {
            var Q0;
            Q0=makeQuery(id+"F30.boolean.opBoolean","MERGE",FACE,{"derivedFrom":[makeQuery(id+"F2.opExtrude","SWEPT_FACE",FACE,{"disambiguationData":[OSD([sQuery(id+"F0.wireOp",EDGE,"E11")])]}),makeQuery(id+"F30.opExtrude","CAP_FACE",FACE,{"disambiguationData":[OSD([sQuery(id+"F29.wireOp",EDGE,"E83.0"),sQuery(id+"F29.wireOp",EDGE,"E86"),sQuery(id+"F29.wireOp",EDGE,"E87"),sQuery(id+"F29.wireOp",EDGE,"E88"),sQuery(id+"F29.wireOp",EDGE,"E89"),sQuery(id+"F29.wireOp",EDGE,"E90"),sQuery(id+"F29.wireOp",EDGE,"E93.filletArc"),sQuery(id+"F29.wireOp",EDGE,"E94.filletArc"),sQuery(id+"F29.wireOp",EDGE,"E95.filletArc")])],"isStart":true}),makeQuery(id+"F30.opExtrude","CAP_FACE",FACE,{"disambiguationData":[OSD([sQuery(id+"F29.wireOp",EDGE,"E96"),sQuery(id+"F29.wireOp",EDGE,"E97"),sQuery(id+"F29.wireOp",EDGE,"E98"),sQuery(id+"F29.wireOp",EDGE,"E99"),sQuery(id+"F29.wireOp",EDGE,"E100"),sQuery(id+"F29.wireOp",EDGE,"E101"),sQuery(id+"F29.wireOp",EDGE,"E102.filletArc"),sQuery(id+"F29.wireOp",EDGE,"E103.filletArc"),sQuery(id+"F29.wireOp",EDGE,"E104.filletArc")])],"isStart":true})]});
            var sketch = newSketch(context, id + "F40", { "sketchPlane" : qUnion([Q0])});
            skLineSegment(sketch, "E139.0", {"start": v(-101, -64) * mm, "end": v(-101, -111) * mm});
            skLineSegment(sketch, "E140.0", {"start": v(-101, 64) * mm, "end": v(-101, 111) * mm});
            skLineSegment(sketch, "E141.0", {"start": v(-55.23, -71) * mm, "end": v(-155.23, -71) * mm});
            skLineSegment(sketch, "E142.0", {"start": v(-55.23, -71) * mm, "end": v(-55.23, -106) * mm});
            skLineSegment(sketch, "E143.0.0", {"start": v(-55.23, -106) * mm, "end": v(-155.23, -106) * mm});
            skLineSegment(sketch, "E143.0.1", {"start": v(-155.23, -106) * mm, "end": v(-155.23, -71) * mm});
            skLineSegment(sketch, "E143.0.2", {"start": v(-155.23, -71) * mm, "end": v(-55.23, -71) * mm});
            skLineSegment(sketch, "E144.0", {"start": v(-55.23, 106) * mm, "end": v(-155.23, 106) * mm});
            skLineSegment(sketch, "E145.0", {"start": v(-55.23, 71) * mm, "end": v(-155.23, 71) * mm});
            skLineSegment(sketch, "E146", {"start": v(-55.23, 106) * mm, "end": v(-55.23, 71) * mm});
            skSolve(sketch);
        }
        {
            var Q0;
            {var subQ5=sQuery(id+"F40.wireOp",EDGE,"E146");Q0=makeQuery(id+"F40.imprint","IMPRINT",FACE,{"disambiguationData":[TD([[makeQuery(id+"F40.imprint","IMPRINT",EDGE,{"derivedFrom":subQ5}),-1.0]])]});}
            var Q1;
            {var subQ5=sQuery(id+"F40.wireOp",EDGE,"E142.0");Q1=makeQuery(id+"F40.imprint","IMPRINT",FACE,{"disambiguationData":[TD([[makeQuery(id+"F40.imprint","IMPRINT",EDGE,{"derivedFrom":subQ5}),-1.0]])]});}
            var Q2;
            {var subQ0=sQuery(id+"F24.wireOp",EDGE,"E70.0");Q2=makeQuery(id+"F26.boolean.opBoolean","MERGE",FACE,{"derivedFrom":[makeQuery(id+"F25.opExtrude","SWEPT_FACE",FACE,{"disambiguationData":[OSD([subQ0])]}),makeQuery(id+"F26.opExtrude","SWEPT_FACE",FACE,{"disambiguationData":[OSD([subQ0])]})]});}
            extrude(context, id + "F41", {"entities" : qUnion([Q0, Q1]), "operationType" : NewBodyOperationType.ADD, "endBound" : BoundingType.UP_TO_SURFACE, "endBoundEntityFace" : qUnion([Q2]), "depth" : 25 * mm});
        }
        {
            var Q0;
            Q0=makeQuery(id+"F19.imprint","IMPRINT",FACE,{"disambiguationData":[TD([[makeQuery(id+"F19.imprint","IMPRINT",EDGE,{"derivedFrom":sQuery(id+"F19.wireOp",EDGE,"E54")}),1.0]])]});
            var Q1;
            Q1=makeQuery(id+"F19.imprint","IMPRINT",FACE,{"disambiguationData":[TD([[makeQuery(id+"F19.imprint","IMPRINT",EDGE,{"derivedFrom":sQuery(id+"F19.wireOp",EDGE,"E56")}),1.0]])]});
            extrude(context, id + "F42", {"entities" : qUnion([Q0, Q1]), "operationType" : NewBodyOperationType.ADD, "endBound" : BoundingType.SYMMETRIC, "depth" : 50 * mm});
        }
    });
